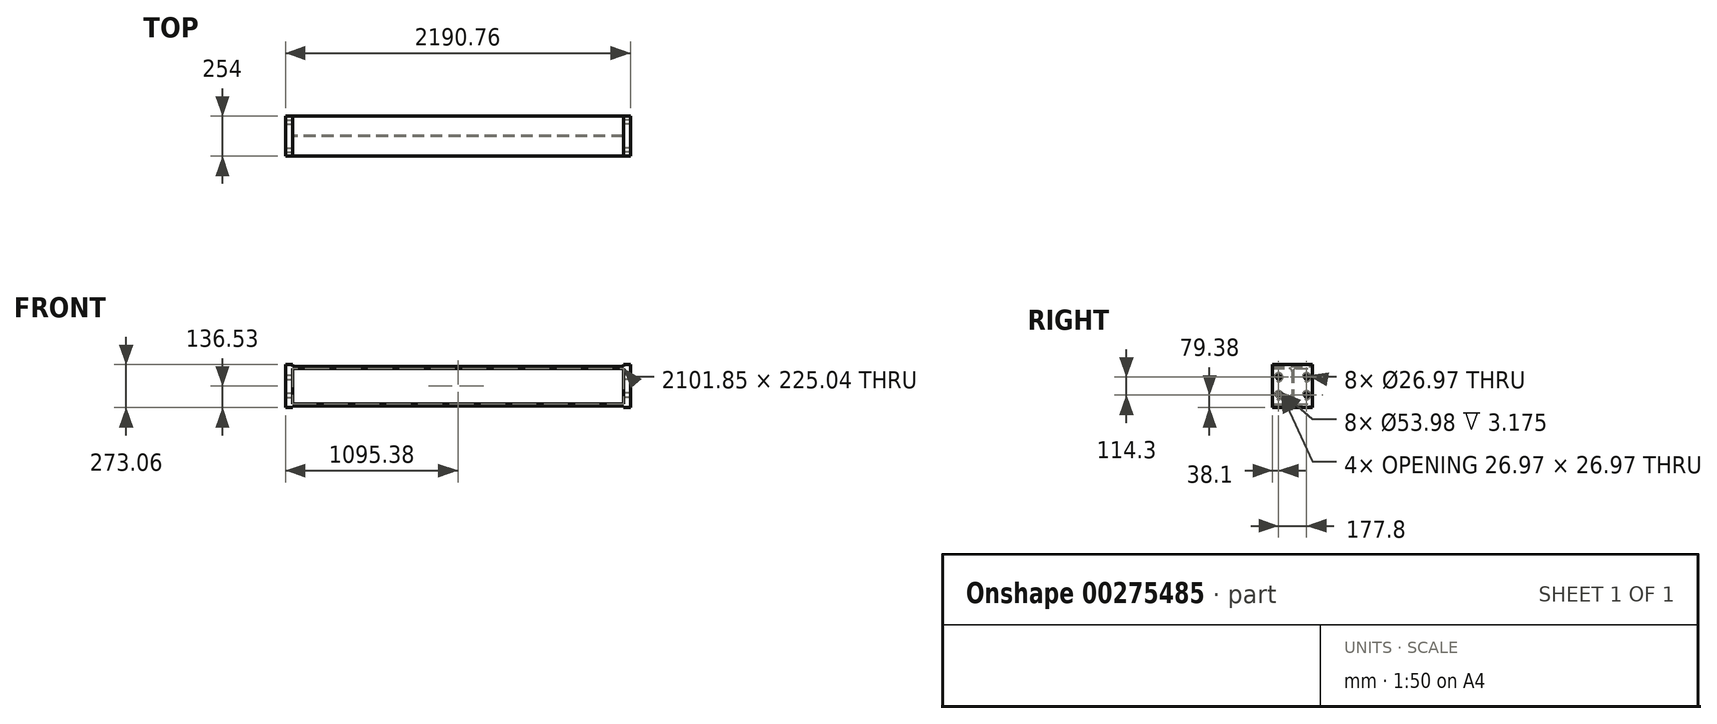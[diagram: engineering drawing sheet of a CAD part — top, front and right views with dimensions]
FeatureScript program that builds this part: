
annotation { "Feature Type Name" : "Feature", "Feature Type Description" : "" }
export const myFeature = defineFeature(function(context is Context, id is Id, definition is map)
    precondition{}
    {
        {
            var Q0;
            Q0=qCreatedBy(makeId("Right.planeOp"),FACE);
            var sketch = newSketch(context, id + "F0", { "sketchPlane" : qUnion([Q0])});
            skLineSegment(sketch, "E0.bottom", {"start": v(-127, 126.75) * mm, "end": v(127, 126.75) * mm});
            skLineSegment(sketch, "E0.top", {"start": v(-127, -126.75) * mm, "end": v(127, -126.75) * mm});
            skLineSegment(sketch, "E0.left", {"start": v(-127, 126.75) * mm, "end": v(-127, 112.52) * mm});
            skLineSegment(sketch, "E0.right", {"start": v(127, 126.75) * mm, "end": v(127, 112.52) * mm});
            skPoint(sketch, "E0.middle", {"position": v(0, 0) * mm});
            skLineSegment(sketch, "E1", {"start": v(0, 126.75) * mm, "end": v(0, -126.75) * mm, "construction": true});
            skLineSegment(sketch, "E2.0", {"start": v(-127, 112.52) * mm, "end": v(-22.1, 112.52) * mm});
            skLineSegment(sketch, "E3.0", {"start": v(-4.32, 94.74) * mm, "end": v(-4.32, -94.74) * mm});
            skLineSegment(sketch, "E4", {"start": v(-178.76, 0) * mm, "end": v(153.27, 0) * mm, "construction": true});
            skLineSegment(sketch, "E5.MirrorCS", {"start": v(-127, -112.52) * mm, "end": v(-22.1, -112.52) * mm});
            skLineSegment(sketch, "E6.MirrorCS", {"start": v(4.32, 94.74) * mm, "end": v(4.32, -94.74) * mm});
            skLineSegment(sketch, "E7.trimOffspring", {"start": v(-127, -112.52) * mm, "end": v(-127, -126.75) * mm});
            skLineSegment(sketch, "E8.trimOffspring", {"start": v(127, -112.52) * mm, "end": v(127, -126.75) * mm});
            skPoint(sketch, "E9.orphan", {"position": v(4.32, 126.75) * mm});
            skPoint(sketch, "E10.orphan", {"position": v(-4.32, 126.75) * mm});
            skLineSegment(sketch, "E11.trimOffspring", {"start": v(22.1, 112.52) * mm, "end": v(127, 112.52) * mm});
            skPoint(sketch, "E12.orphan", {"position": v(4.32, -126.75) * mm});
            skLineSegment(sketch, "E13.trimOffspring", {"start": v(22.1, -112.52) * mm, "end": v(127, -112.52) * mm});
            skPoint(sketch, "E14.orphan", {"position": v(-4.32, -126.75) * mm});
            skPoint(sketch, "E15.visualSharp", {"position": v(-4.32, -112.52) * mm});
            skArc(sketch, "E15.filletArc", {"start": v(-22.1, -112.52) * mm, "mid": v(-9.53, -107.31) * mm, "end": v(-4.32, -94.74) * mm});
            skPoint(sketch, "E16.visualSharp", {"position": v(4.32, -112.52) * mm});
            skArc(sketch, "E16.filletArc", {"start": v(4.32, -94.74) * mm, "mid": v(9.53, -107.31) * mm, "end": v(22.1, -112.52) * mm});
            skPoint(sketch, "E17.visualSharp", {"position": v(-4.32, 112.52) * mm});
            skArc(sketch, "E17.filletArc", {"start": v(-4.32, 94.74) * mm, "mid": v(-9.53, 107.31) * mm, "end": v(-22.1, 112.52) * mm});
            skPoint(sketch, "E18.visualSharp", {"position": v(4.32, 112.52) * mm});
            skArc(sketch, "E18.filletArc", {"start": v(22.1, 112.52) * mm, "mid": v(9.53, 107.31) * mm, "end": v(4.32, 94.74) * mm});
            skSolve(sketch);
        }
        {
            var Q0;
            Q0 = qSketchRegion(id + "F0", true);
            extrude(context, id + "F1", {"entities" : qUnion([Q0]), "endBound" : BoundingType.SYMMETRIC, "depth" : 2101.85 * mm});
        }
        {
            var Q0;
            Q0=makeQuery(id+"F1.opExtrude","CAP_FACE",FACE,{"disambiguationData":[OSD([sQuery(id+"F0.wireOp",EDGE,"E0.bottom"),sQuery(id+"F0.wireOp",EDGE,"E0.top"),sQuery(id+"F0.wireOp",EDGE,"E0.left"),sQuery(id+"F0.wireOp",EDGE,"E0.right"),sQuery(id+"F0.wireOp",EDGE,"E2.0"),sQuery(id+"F0.wireOp",EDGE,"E3.0"),sQuery(id+"F0.wireOp",EDGE,"E5.MirrorCS"),sQuery(id+"F0.wireOp",EDGE,"E6.MirrorCS"),sQuery(id+"F0.wireOp",EDGE,"E7.trimOffspring"),sQuery(id+"F0.wireOp",EDGE,"E8.trimOffspring"),sQuery(id+"F0.wireOp",EDGE,"E11.trimOffspring"),sQuery(id+"F0.wireOp",EDGE,"E13.trimOffspring"),sQuery(id+"F0.wireOp",EDGE,"E15.filletArc"),sQuery(id+"F0.wireOp",EDGE,"E16.filletArc"),sQuery(id+"F0.wireOp",EDGE,"E17.filletArc"),sQuery(id+"F0.wireOp",EDGE,"E18.filletArc")])],"isStart":false});
            var sketch = newSketch(context, id + "F2", { "sketchPlane" : qUnion([Q0])});
            skLineSegment(sketch, "E19", {"start": v(0, 126.75) * mm, "end": v(0, -126.75) * mm, "construction": true});
            skLineSegment(sketch, "E20.bottom", {"start": v(-127, 136.53) * mm, "end": v(127, 136.53) * mm});
            skLineSegment(sketch, "E20.top", {"start": v(-127, -136.53) * mm, "end": v(127, -136.53) * mm});
            skLineSegment(sketch, "E20.left", {"start": v(-127, 136.53) * mm, "end": v(-127, -136.53) * mm});
            skLineSegment(sketch, "E20.right", {"start": v(127, 136.53) * mm, "end": v(127, -136.53) * mm});
            skPoint(sketch, "E20.middle", {"position": v(0, 0) * mm});
            skSolve(sketch);
        }
        {
            var Q0;
            Q0 = qSketchRegion(id + "F2", true);
            extrude(context, id + "F3", {"entities" : qUnion([Q0]), "depth" : 44.45 * mm});
        }
        {
            var Q0;
            Q0=makeQuery(id+"F3.opExtrude","CAP_FACE",FACE,{"disambiguationData":[OSD([sQuery(id+"F2.wireOp",EDGE,"E20.bottom"),sQuery(id+"F2.wireOp",EDGE,"E20.top"),sQuery(id+"F2.wireOp",EDGE,"E20.left"),sQuery(id+"F2.wireOp",EDGE,"E20.right")])],"isStart":true});
            var sketch = newSketch(context, id + "F4", { "sketchPlane" : qUnion([Q0])});
            skLineSegment(sketch, "E21", {"start": v(0, 177) * mm, "end": v(0, -169.58) * mm, "construction": true});
            skPoint(sketch, "E21.startSnap0", {"position": v(0, 136.53) * mm});
            skLineSegment(sketch, "E22", {"start": v(-180.1, 0) * mm, "end": v(172.67, 0) * mm, "construction": true});
            skLineSegment(sketch, "E23.0", {"start": v(-180.1, 57.15) * mm, "end": v(172.67, 57.15) * mm, "construction": true});
            skLineSegment(sketch, "E24.0", {"start": v(-88.9, 177) * mm, "end": v(-88.9, -169.58) * mm, "construction": true});
            skPoint(sketch, "E25", {"position": v(-88.9, 57.15) * mm});
            skPoint(sketch, "E26.MirrorP", {"position": v(-88.9, -57.15) * mm});
            skPoint(sketch, "E27.MirrorP", {"position": v(88.9, 57.15) * mm});
            skPoint(sketch, "E28.MirrorP", {"position": v(88.9, -57.15) * mm});
            skSolve(sketch);
        }
        {
            var Q0;
            Q0=sQuery(id+"F4.wireOp",VERTEX,"E25");
            var Q1;
            Q1=sQuery(id+"F4.wireOp",VERTEX,"E26.MirrorP");
            var Q2;
            Q2=sQuery(id+"F4.wireOp",VERTEX,"E27.MirrorP");
            var Q3;
            Q3=sQuery(id+"F4.wireOp",VERTEX,"E28.MirrorP");
            var Q4;
            Q4=makeQuery(id+"F3.opExtrude","SWEPT_BODY",BODY,{"disambiguationData":[OSD([sQuery(id+"F2.wireOp",EDGE,"E20.bottom"),sQuery(id+"F2.wireOp",EDGE,"E20.top"),sQuery(id+"F2.wireOp",EDGE,"E20.left"),sQuery(id+"F2.wireOp",EDGE,"E20.right")])]});
            hole(context, id + "F5", {"style" : HoleStyle.C_BORE, "endStyle" : HoleEndStyle.THROUGH, "holeDiameter" : 26.97 * mm, "cBoreDiameter" : 53.97 * mm, "cBoreDepth" : 3.17 * mm, "tappedDepth" : 24.82 * mm, "tapClearance" : 3, "startFromSketch" : true, "locations" : qUnion([Q0, Q1, Q2, Q3]), "scope" : qUnion([Q4])});
        }
        {
            var Q0;
            Q0=makeQuery(id+"F3.opExtrude","SWEPT_BODY",BODY,{"disambiguationData":[OSD([sQuery(id+"F2.wireOp",EDGE,"E20.bottom"),sQuery(id+"F2.wireOp",EDGE,"E20.top"),sQuery(id+"F2.wireOp",EDGE,"E20.left"),sQuery(id+"F2.wireOp",EDGE,"E20.right")])]});
            var Q1;
            Q1=qCreatedBy(makeId("Right.planeOp"),FACE);
            mirror(context, id + "F6", {"operationType" : NewBodyOperationType.ADD, "entities" : qUnion([Q0]), "mirrorPlane" : qUnion([Q1])});
        }
    });
